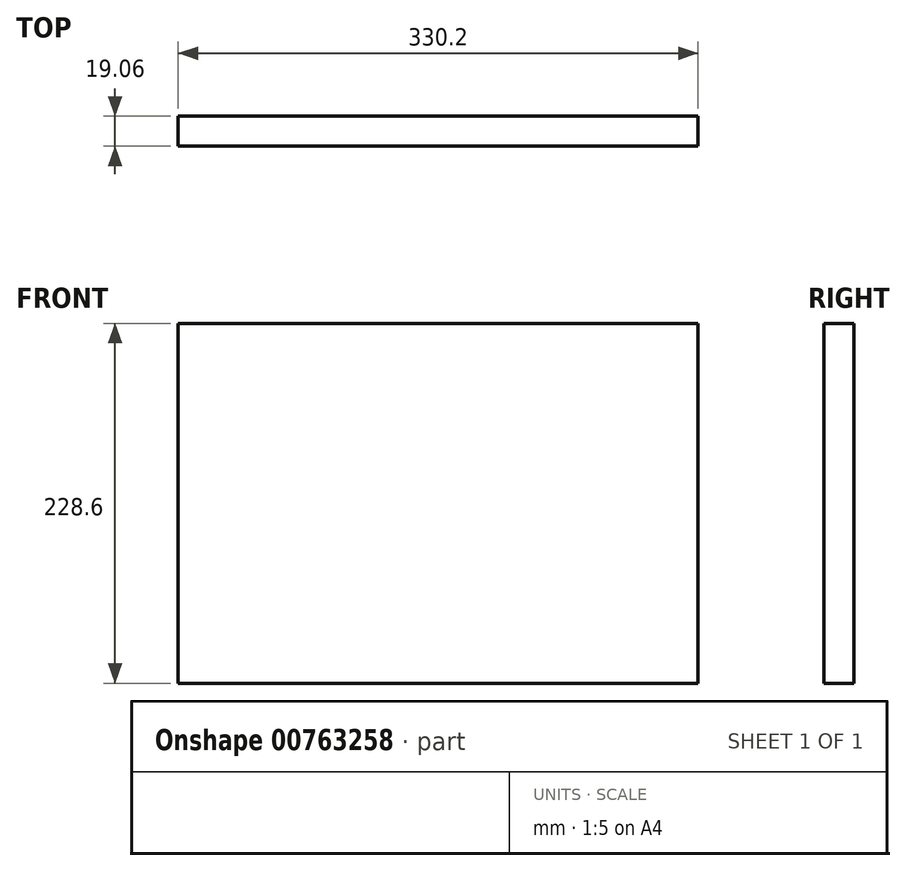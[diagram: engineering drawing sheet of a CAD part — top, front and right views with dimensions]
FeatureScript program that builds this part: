
annotation { "Feature Type Name" : "Feature", "Feature Type Description" : "" }
export const myFeature = defineFeature(function(context is Context, id is Id, definition is map)
    precondition{}
    {
        {
            var Q0;
            Q0=qCreatedBy(makeId("Top.planeOp"),FACE);
            var sketch = newSketch(context, id + "F0", { "sketchPlane" : qUnion([Q0])});
            skLineSegment(sketch, "E0.bottom", {"start": v(165.1, 9.53) * mm, "end": v(-165.1, 9.53) * mm});
            skLineSegment(sketch, "E0.top", {"start": v(165.1, -9.53) * mm, "end": v(-165.1, -9.53) * mm});
            skLineSegment(sketch, "E0.left", {"start": v(165.1, 9.53) * mm, "end": v(165.1, -9.53) * mm});
            skLineSegment(sketch, "E0.right", {"start": v(-165.1, 9.53) * mm, "end": v(-165.1, -9.53) * mm});
            skPoint(sketch, "E0.middle", {"position": v(0, 0) * mm});
            skSolve(sketch);
        }
        {
            var Q0;
            Q0 = qSketchRegion(id + "F0", true);
            extrude(context, id + "F1", {"entities" : qUnion([Q0]), "depth" : 228.6 * mm, "offsetDistance" : 25.4 * mm});
        }
    });
